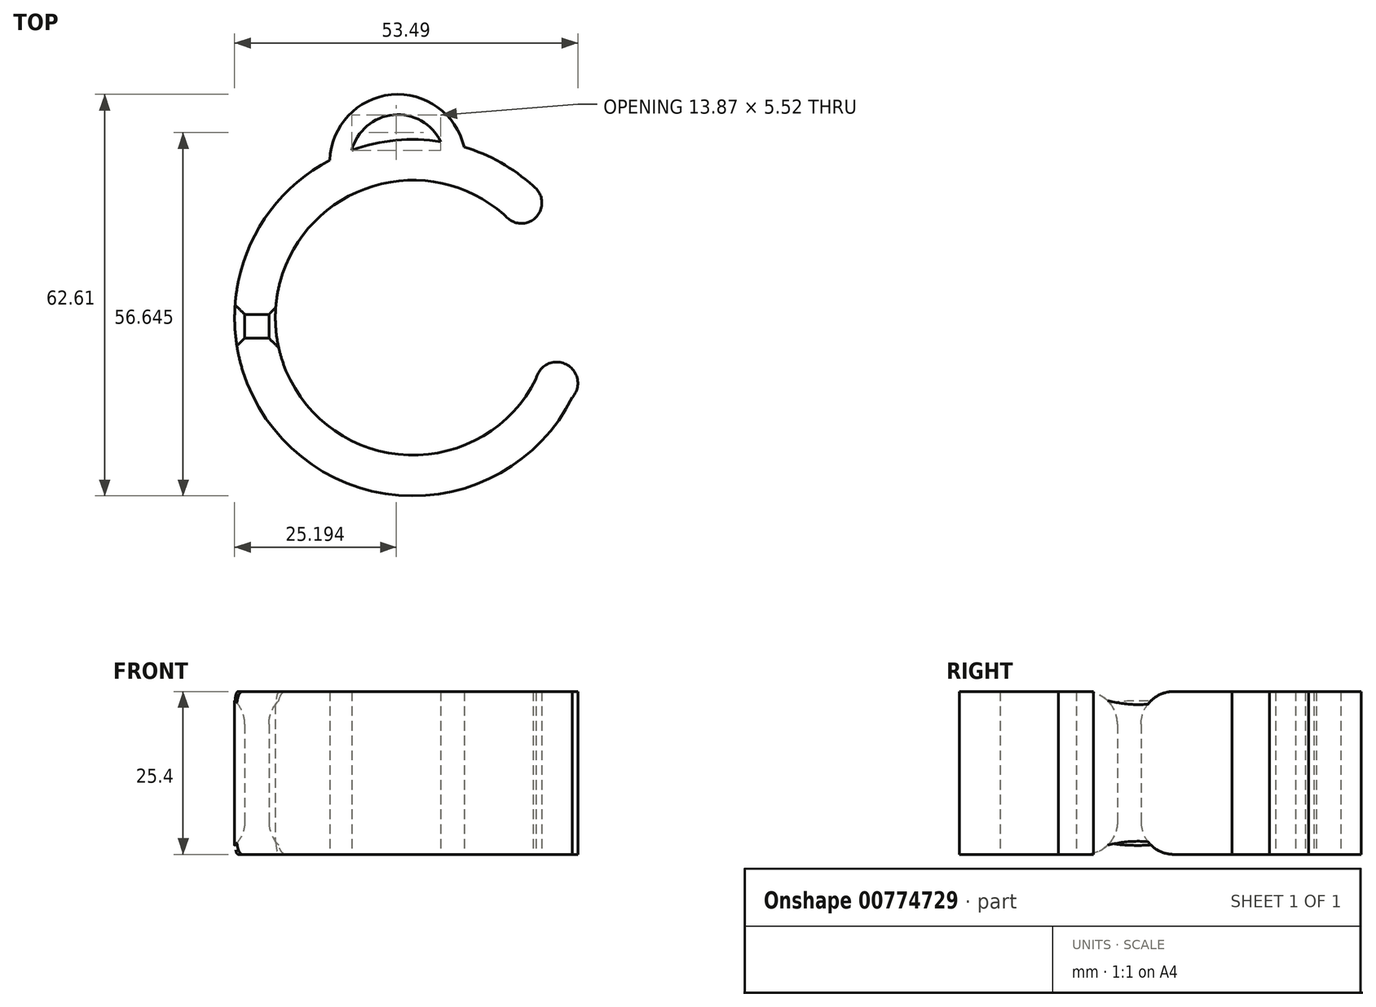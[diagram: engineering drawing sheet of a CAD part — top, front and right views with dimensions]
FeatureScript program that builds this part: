
annotation { "Feature Type Name" : "Feature", "Feature Type Description" : "" }
export const myFeature = defineFeature(function(context is Context, id is Id, definition is map)
    precondition{}
    {
        {
            var Q0;
            Q0=qCreatedBy(makeId("Top.planeOp"),FACE);
            var sketch = newSketch(context, id + "F0", { "sketchPlane" : qUnion([Q0])});
            skArc(sketch, "E0", {"start": v(16.48, 13.63) * mm, "mid": v(-18.7, -6.6) * mm, "end": v(21.52, -12.04) * mm});
            skArc(sketch, "E1.0", {"start": v(21.06, 18.06) * mm, "mid": v(-24.97, -7.57) * mm, "end": v(27.2, -14.88) * mm});
            skArc(sketch, "E2", {"start": v(16.9, 13.22) * mm, "mid": v(21.67, 13.34) * mm, "end": v(21.06, 18.06) * mm});
            skArc(sketch, "E3", {"start": v(27.2, -14.88) * mm, "mid": v(26.21, -9.74) * mm, "end": v(21.52, -12.04) * mm});
            skPoint(sketch, "E4.visualSharp", {"position": v(16.78, 13.36) * mm});
            skArc(sketch, "E4.filletArc", {"start": v(16.9, 13.22) * mm, "mid": v(16.7, 13.43) * mm, "end": v(16.48, 13.63) * mm});
            skLineSegment(sketch, "E5.bottom", {"start": v(-23.87, -1.97) * mm, "end": v(-20.1, -1.97) * mm});
            skLineSegment(sketch, "E5.top", {"start": v(-23.87, -5.65) * mm, "end": v(-20.1, -5.65) * mm});
            skLineSegment(sketch, "E5.left", {"start": v(-23.87, -1.97) * mm, "end": v(-23.87, -5.65) * mm});
            skLineSegment(sketch, "E5.right", {"start": v(-20.1, -1.97) * mm, "end": v(-20.1, -5.65) * mm});
            skSolve(sketch);
        }
        {
            var Q0;
            Q0=makeQuery(id+"F0.imprint","IMPRINT",FACE,{"disambiguationData":[TD([[makeQuery(id+"F0.imprint","IMPRINT",EDGE,{"derivedFrom":sQuery(id+"F0.wireOp",EDGE,"E0")}),-1.0]])]});
            extrude(context, id + "F1", {"entities" : qUnion([Q0]), "depth" : 25.4 * mm, "offsetDistance" : 25.4 * mm});
        }
        {
            var Q0;
            Q0=qCreatedBy(makeId("Top.planeOp"),FACE);
            var sketch = newSketch(context, id + "F2", { "sketchPlane" : qUnion([Q0])});
            skArc(sketch, "E6", {"start": v(6.74, 24.85) * mm, "mid": v(-1.47, 29.04) * mm, "end": v(-7.43, 22) * mm});
            skArc(sketch, "E7.0", {"start": v(10.38, 23.82) * mm, "mid": v(-1.36, 32.27) * mm, "end": v(-10.59, 21.13) * mm});
            skArc(sketch, "E8.0", {"start": v(21.06, 18.06) * mm, "mid": v(-24.97, -7.57) * mm, "end": v(27.2, -14.88) * mm});
            skSolve(sketch);
        }
        {
            var Q0;
            {var subQ0=sQuery(id+"F2.wireOp",EDGE,"E8.0");var subQ1=sQuery(id+"F2.wireOp",EDGE,"E6");var subQ2=makeQuery(id+"F2.imprint","INTERSECT",VERTEX,{"disambiguationData":[OD(0.0)],"derivedFrom":[subQ1,subQ0]});Q0=makeQuery(id+"F2.imprint","IMPRINT",FACE,{"disambiguationData":[TD([[makeQuery(id+"F2.imprint","IMPRINT",EDGE,{"disambiguationData":[TD([[subQ2,-1.0]])],"derivedFrom":subQ1}),-1.0]])]});}
            extrude(context, id + "F3", {"entities" : qUnion([Q0]), "operationType" : NewBodyOperationType.ADD, "depth" : 25.4 * mm, "offsetDistance" : 25.4 * mm});
        }
        {
            var Q0;
            Q0=makeQuery(id+"F1.opExtrude","CAP_EDGE",EDGE,{"disambiguationData":[OSD([sQuery(id+"F0.wireOp",EDGE,"E5.right")])],"isStart":false});
            fillet(context, id + "F4", {"entities" : qUnion([Q0]), "radius" : 5.08 * mm, "tangentPropagation" : true, "allowEdgeOverflow" : false});
        }
        {
            var Q0;
            Q0=makeQuery(id+"F1.opExtrude","CAP_EDGE",EDGE,{"disambiguationData":[OSD([sQuery(id+"F0.wireOp",EDGE,"E5.left")])],"isStart":false});
            fillet(context, id + "F5", {"entities" : qUnion([Q0]), "radius" : 5.08 * mm, "tangentPropagation" : true, "allowEdgeOverflow" : false});
        }
        {
            var Q0;
            Q0=makeQuery(id+"F1.opExtrude","CAP_EDGE",EDGE,{"disambiguationData":[OSD([sQuery(id+"F0.wireOp",EDGE,"E5.bottom")])],"isStart":false});
            var Q1;
            Q1=makeQuery(id+"F1.opExtrude","CAP_EDGE",EDGE,{"disambiguationData":[OSD([sQuery(id+"F0.wireOp",EDGE,"E5.top")])],"isStart":false});
            fillet(context, id + "F6", {"entities" : qUnion([Q0, Q1]), "radius" : 5.08 * mm, "tangentPropagation" : true, "allowEdgeOverflow" : false});
        }
        {
            var Q0;
            Q0=makeQuery(id+"F1.opExtrude","CAP_EDGE",EDGE,{"disambiguationData":[OSD([sQuery(id+"F0.wireOp",EDGE,"E5.left")])],"isStart":true});
            var Q1;
            Q1=makeQuery(id+"F1.opExtrude","CAP_EDGE",EDGE,{"disambiguationData":[OSD([sQuery(id+"F0.wireOp",EDGE,"E5.right")])],"isStart":true});
            var Q2;
            Q2=makeQuery(id+"F1.opExtrude","CAP_EDGE",EDGE,{"disambiguationData":[OSD([sQuery(id+"F0.wireOp",EDGE,"E5.top")])],"isStart":true});
            var Q3;
            Q3=makeQuery(id+"F1.opExtrude","CAP_EDGE",EDGE,{"disambiguationData":[OSD([sQuery(id+"F0.wireOp",EDGE,"E5.bottom")])],"isStart":true});
            fillet(context, id + "F7", {"entities" : qUnion([Q0, Q1, Q2, Q3]), "radius" : 5.08 * mm, "tangentPropagation" : true, "allowEdgeOverflow" : false});
        }
    });
